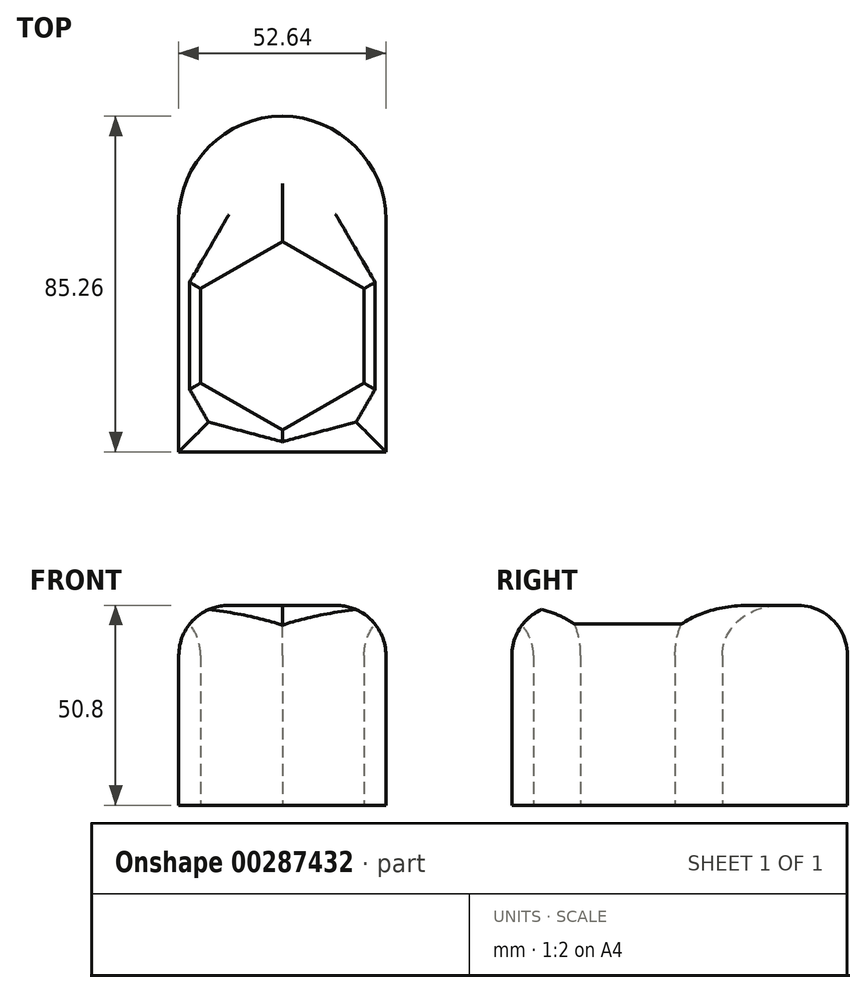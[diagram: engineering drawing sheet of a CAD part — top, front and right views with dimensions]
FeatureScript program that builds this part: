
annotation { "Feature Type Name" : "Feature", "Feature Type Description" : "" }
export const myFeature = defineFeature(function(context is Context, id is Id, definition is map)
    precondition{}
    {
        {
            var Q0;
            Q0=qCreatedBy(makeId("Top.planeOp"),FACE);
            var sketch = newSketch(context, id + "F0", { "sketchPlane" : qUnion([Q0])});
            skLineSegment(sketch, "E0.bottom", {"start": v(26.32, -29.47) * mm, "end": v(-26.32, -29.47) * mm});
            skLineSegment(sketch, "E0.left", {"start": v(26.32, -29.47) * mm, "end": v(26.32, 29.47) * mm});
            skLineSegment(sketch, "E0.right", {"start": v(-26.32, -29.47) * mm, "end": v(-26.32, 29.47) * mm});
            skPoint(sketch, "E0.middle", {"position": v(0, 0) * mm});
            skArc(sketch, "E1", {"start": v(26.32, 29.47) * mm, "mid": v(0, 55.8) * mm, "end": v(-26.32, 29.47) * mm});
            skCircle(sketch, "E2.cCircle", {"center": v(0, 0) * mm, "radius": 20.77 * mm, "construction": true});
            skLineSegment(sketch, "E2.0", {"start": v(20.77, 12) * mm, "end": v(20.77, -12) * mm});
            skLineSegment(sketch, "E2.1", {"start": v(20.77, -12) * mm, "end": v(0, -23.99) * mm});
            skLineSegment(sketch, "E2.2", {"start": v(0, -23.99) * mm, "end": v(-20.77, -12) * mm});
            skLineSegment(sketch, "E2.3", {"start": v(-20.77, -12) * mm, "end": v(-20.77, 12) * mm});
            skLineSegment(sketch, "E2.4", {"start": v(-20.77, 12) * mm, "end": v(0, 23.99) * mm});
            skLineSegment(sketch, "E2.5", {"start": v(0, 23.99) * mm, "end": v(20.77, 12) * mm});
            skPoint(sketch, "E2.0.midPoint", {"position": v(20.77, 0) * mm});
            skSolve(sketch);
        }
        {
            var Q0;
            Q0=makeQuery(id+"F0.imprint","IMPRINT",FACE,{"disambiguationData":[TD([[makeQuery(id+"F0.imprint","IMPRINT",EDGE,{"derivedFrom":sQuery(id+"F0.wireOp",EDGE,"E0.bottom")}),-1.0]])]});
            var Q1;
            Q1=makeQuery(id+"F0.imprint","IMPRINT",FACE,{"disambiguationData":[TD([[makeQuery(id+"F0.imprint","IMPRINT",EDGE,{"derivedFrom":sQuery(id+"F0.wireOp",EDGE,"E0.top")}),-1.0]])]});
            extrude(context, id + "F1", {"entities" : qUnion([Q0, Q1]), "depth" : 50.8 * mm});
        }
        {
            var Q0;
            Q0=makeQuery(id+"F1.opExtrude","CAP_FACE",FACE,{"disambiguationData":[OSD([sQuery(id+"F0.wireOp",EDGE,"E0.bottom"),sQuery(id+"F0.wireOp",EDGE,"E0.top"),sQuery(id+"F0.wireOp",EDGE,"E0.left"),sQuery(id+"F0.wireOp",EDGE,"E0.right")])],"isStart":false});
            fillet(context, id + "F2", {"entities" : qUnion([Q0]), "radius" : 12.7 * mm, "tangentPropagation" : true, "allowEdgeOverflow" : false});
        }
    });
